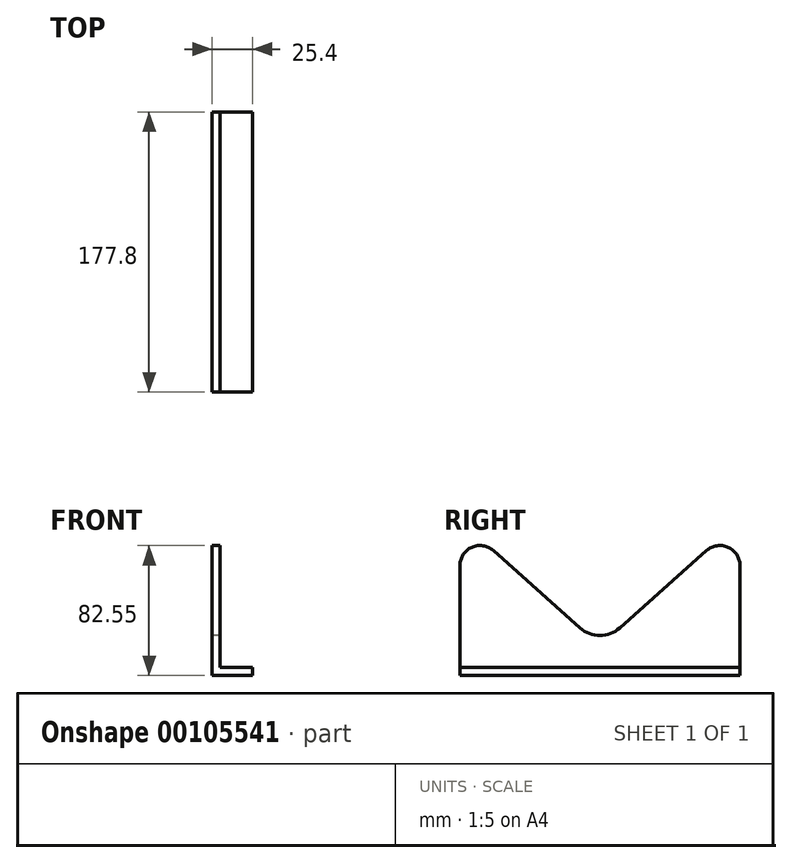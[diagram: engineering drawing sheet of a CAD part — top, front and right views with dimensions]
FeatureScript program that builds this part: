
annotation { "Feature Type Name" : "Feature", "Feature Type Description" : "" }
export const myFeature = defineFeature(function(context is Context, id is Id, definition is map)
    precondition{}
    {
        {
            var Q0;
            Q0=qCreatedBy(makeId("Front.planeOp"),FACE);
            var sketch = newSketch(context, id + "F0", { "sketchPlane" : qUnion([Q0])});
            skLineSegment(sketch, "E0", {"start": v(0, 0) * mm, "end": v(0, 82.55) * mm});
            skLineSegment(sketch, "E1", {"start": v(0, 82.55) * mm, "end": v(5.08, 82.55) * mm});
            skLineSegment(sketch, "E2", {"start": v(5.08, 82.55) * mm, "end": v(5.08, 5.08) * mm});
            skLineSegment(sketch, "E3", {"start": v(5.08, 5.08) * mm, "end": v(25.4, 5.08) * mm});
            skLineSegment(sketch, "E4", {"start": v(25.4, 5.08) * mm, "end": v(25.4, 0) * mm});
            skLineSegment(sketch, "E5", {"start": v(25.4, 0) * mm, "end": v(0, 0) * mm});
            skSolve(sketch);
        }
        {
            var Q0;
            Q0 = qSketchRegion(id + "F0", true);
            extrude(context, id + "F1", {"entities" : qUnion([Q0]), "depth" : 177.8 * mm});
        }
        {
            var Q0;
            Q0=makeQuery(id+"F1.opExtrude","SWEPT_FACE",FACE,{"disambiguationData":[OSD([sQuery(id+"F0.wireOp",EDGE,"E0")])]});
            var sketch = newSketch(context, id + "F2", { "sketchPlane" : qUnion([Q0])});
            skCircle(sketch, "E6", {"center": v(165.1, 69.85) * mm, "radius": 2.29 * mm});
            skCircle(sketch, "E7", {"center": v(12.7, 69.85) * mm, "radius": 3.18 * mm});
            skSolve(sketch);
        }
        {
            var Q0;
            Q0=makeQuery(id+"F2.imprint","IMPRINT",FACE,{"disambiguationData":[TD([[makeQuery(id+"F2.imprint","IMPRINT",EDGE,{"derivedFrom":sQuery(id+"F2.wireOp",EDGE,"E6")}),-1.0]])]});
            var sketch = newSketch(context, id + "F3", { "sketchPlane" : qUnion([Q0])});
            skArc(sketch, "E8", {"start": v(21.15, 79.33) * mm, "mid": v(7.5, 81.44) * mm, "end": v(0, 69.85) * mm});
            skArc(sketch, "E9", {"start": v(177.8, 69.85) * mm, "mid": v(170.3, 81.44) * mm, "end": v(156.65, 79.33) * mm});
            skArc(sketch, "E10", {"start": v(76.22, 30.23) * mm, "mid": v(88.9, 25.4) * mm, "end": v(101.58, 30.23) * mm});
            skLineSegment(sketch, "E11", {"start": v(21.15, 79.33) * mm, "end": v(76.22, 30.23) * mm});
            skLineSegment(sketch, "E12", {"start": v(156.65, 79.33) * mm, "end": v(101.58, 30.23) * mm});
            skLineSegment(sketch, "E13", {"start": v(177.8, 69.85) * mm, "end": v(203.2, 69.85) * mm});
            skLineSegment(sketch, "E14", {"start": v(203.2, 69.85) * mm, "end": v(203.2, 95.25) * mm});
            skLineSegment(sketch, "E15", {"start": v(203.2, 95.25) * mm, "end": v(-25.4, 95.25) * mm});
            skLineSegment(sketch, "E16", {"start": v(-25.4, 95.25) * mm, "end": v(-25.4, 69.85) * mm});
            skLineSegment(sketch, "E17", {"start": v(-25.4, 69.85) * mm, "end": v(0, 69.85) * mm});
            skSolve(sketch);
        }
        {
            var Q0;
            Q0 = qSketchRegion(id + "F3", true);
            extrude(context, id + "F4", {"entities" : qUnion([Q0]), "operationType" : NewBodyOperationType.REMOVE, "oppositeDirection" : true, "depth" : 25.4 * mm});
        }
    });
